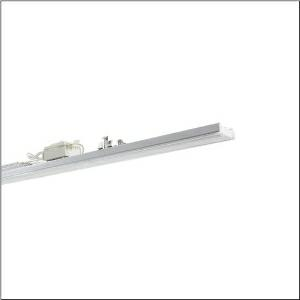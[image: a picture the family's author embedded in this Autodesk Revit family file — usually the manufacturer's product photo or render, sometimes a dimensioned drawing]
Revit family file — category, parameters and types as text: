
# Revit family: licross_r__21_recessed_mo_52te12dn4axg3s4_eb36
name_source: partatom
category: Lighting Fixtures
units: mm (PartAtom-declared; Revit-internal decimal feet)

## family parameters
Cut with Voids When Loaded = No
Host = Face
Light Source = No
Part Type = Normal
Room Calculation Point = No
Round Connector Dimension = Use Diameter
Shared = No

## types (1)
- --- (1 x LED, 950 lm, 6.7 W, 4000K)
    Apparent Load = 7 VA
    CIE Flux Codes = 72 92 99 100 100
    Color Rendering = 80
    Color Temperature = 4000K
    Default Elevation = 1800 mm
    Description = Licross® 21 Recessed MO, luminaire insert, of sheet steel, galvanised, coil coated, white, length: 1.500mm, width: 66mm, height: 67mm, LED rated luminous flux: 10.280lm, light colour: 840, control gear: DALI 2, with plug, 6-pole, with phase selection, for trunking rail, 9 or 11-core, mains connection: 220..240V, AC, 50/60Hz, rated input power: 62W, internal wiring halogen-free, for emergency light function, for trunking rail, 9-/11-core, converter,control gear: single battery element, battery: LiFePO4, 9Ah, primary optical cover: cover, of PMMA, light emission: direct distribution, primary light characteristic: symmetric, protection rating (complete): IP54, insulation class (complete): insulation class I (protective earthing), certification: CE, UKCA, protection symbol: D if used in an environment with non-conductive dust loads with corresponding accessories, impact resistance: IK06, permissible ambient temperature for indoor applications: +5..+35°C, standard: EN 60598-2-22, LABS conformity tested according to VDMA 24364:2018-05, reducing of maximum allowable ambient temperature of 5°C with ceiling mounting, corresponds to IFS (International Featured Standards) requirements for safety and quality in the food industry, packaging unit: 1 piece
    Height = 58 mm
    Lamp = 1 x LED
    Lamp Light Flux = 950 lm
    Lamp Power = 6.7 W
    Lamp count = 1
    Length = 1500 mm
    Luminous efficacy = 142 lm/W
    Manufacturer = Siteco
    ModVariant = No
    Model = 52TE12DN4AXG3S4
    Mounting Place = Ceiling
    Mounting Type = Pendant
    Number of Poles = 1
    OnlyDefault = Yes
    Power Factor = 1
    Product Name = Licross® 21 Recessed MO
    Product group = luminaire insert | ceiling pendant
    ProductGroupID = 902
    Protection Class = Protection class I
    Protection Degree = IP 54
    RLX_Detail_Level = 1
    RLX_Emergency_Light_Flux = 0 lm
    RLX_Emergency_Type = 0
    RLX_Emergency_Type_DB = No
    RlxData = <blob elided: 25013 chars, md5=3b91299f>
    Socket = socket
    Standby Power = 0 W
    System Light Flux = 950 lm
    System Power = 7 W
    Type Comments = : emergency light operation: 3 h
    Type Image = l_1296930.jpg
    URL = http://relux.com
    VarID = @adj_131527
    Voltage = 0 V
    Weight = 0.00 kg
    Width = 66 mm

## geometry (parser evidence)
native form markers: Blend x4, Sweep x9
no freeform markers — native parametric forms only
